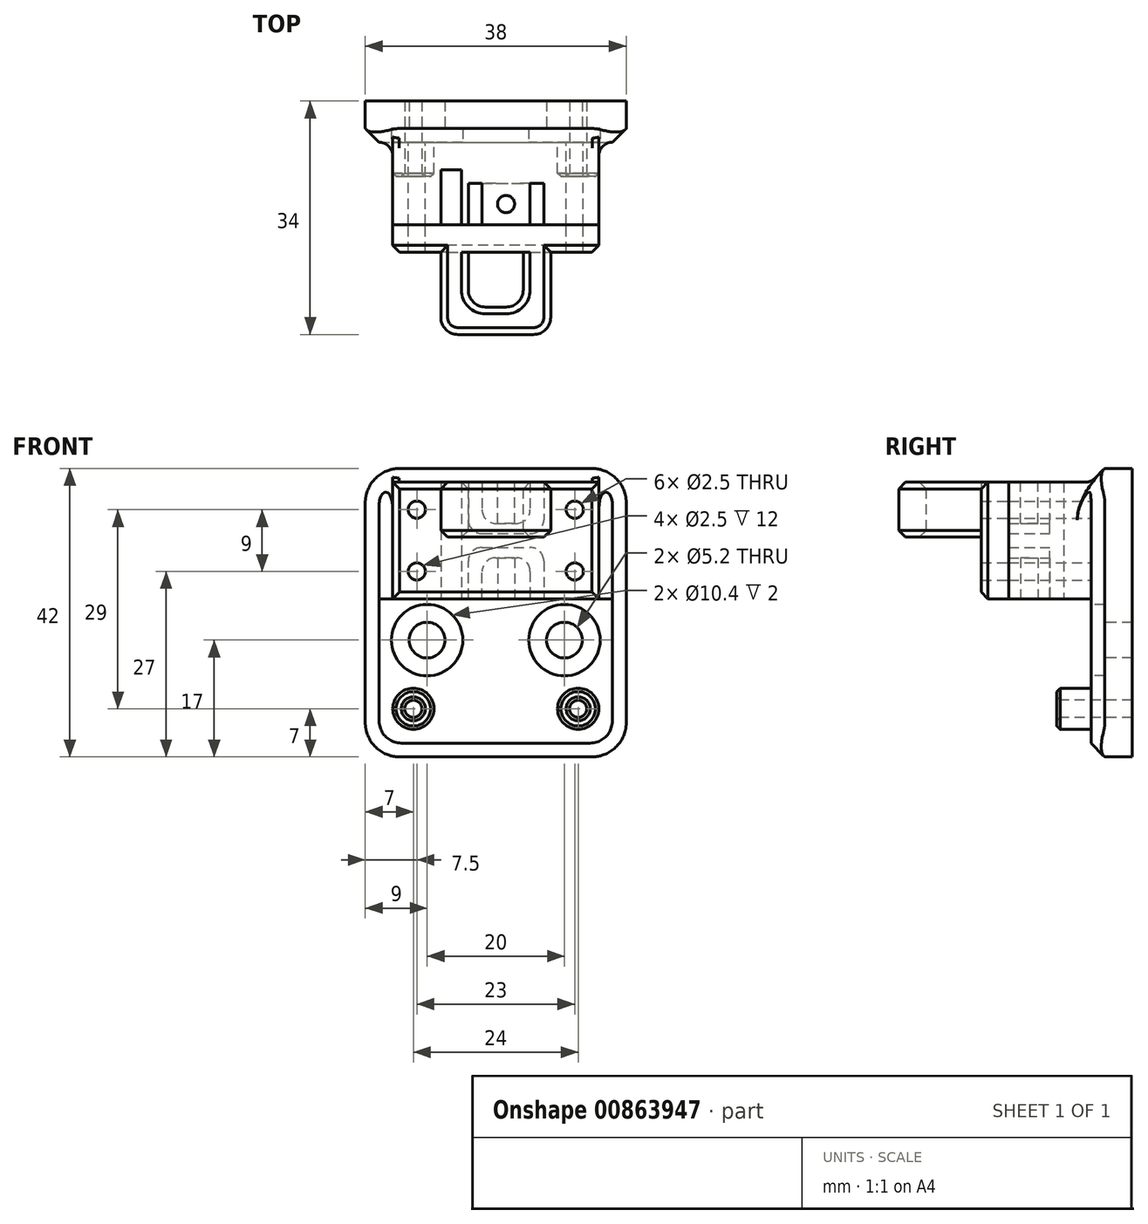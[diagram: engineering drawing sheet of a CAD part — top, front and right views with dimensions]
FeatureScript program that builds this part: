
annotation { "Feature Type Name" : "Feature", "Feature Type Description" : "" }
export const myFeature = defineFeature(function(context is Context, id is Id, definition is map)
    precondition{}
    {
        {
            var Q0;
            Q0=qCreatedBy(makeId("Front.planeOp"),FACE);
            var sketch = newSketch(context, id + "F0", { "sketchPlane" : qUnion([Q0])});
            skLineSegment(sketch, "E0.bottom", {"start": v(-19, 25) * mm, "end": v(19, 25) * mm});
            skLineSegment(sketch, "E0.top", {"start": v(-19, -17) * mm, "end": v(19, -17) * mm});
            skLineSegment(sketch, "E0.left", {"start": v(-19, 25) * mm, "end": v(-19, -17) * mm});
            skLineSegment(sketch, "E0.right", {"start": v(19, 25) * mm, "end": v(19, -17) * mm});
            skCircle(sketch, "E1", {"center": v(-10, 0) * mm, "radius": 2.6 * mm});
            skCircle(sketch, "E2", {"center": v(10, 0) * mm, "radius": 2.6 * mm});
            skCircle(sketch, "E3", {"center": v(-12, -10) * mm, "radius": 3 * mm});
            skCircle(sketch, "E4", {"center": v(-12, -10) * mm, "radius": 1.25 * mm});
            skCircle(sketch, "E5", {"center": v(12, -10) * mm, "radius": 3 * mm});
            skCircle(sketch, "E6", {"center": v(12, -10) * mm, "radius": 1.25 * mm});
            skLineSegment(sketch, "E7", {"start": v(-12, -10) * mm, "end": v(12, -10) * mm, "construction": true});
            skLineSegment(sketch, "E8", {"start": v(-10, 0) * mm, "end": v(10, 0) * mm, "construction": true});
            skLineSegment(sketch, "E9", {"start": v(0, 0) * mm, "end": v(0, -10) * mm, "construction": true});
            skCircle(sketch, "E10", {"center": v(-10, 0) * mm, "radius": 5.2 * mm});
            skCircle(sketch, "E11", {"center": v(10, 0) * mm, "radius": 5.2 * mm});
            skLineSegment(sketch, "E12", {"start": v(0, 25) * mm, "end": v(0, -17) * mm, "construction": true});
            skLineSegment(sketch, "E13.bottom", {"start": v(-15, 23) * mm, "end": v(-8, 23) * mm});
            skLineSegment(sketch, "E13.top", {"start": v(-15, 6) * mm, "end": v(-8, 6) * mm});
            skLineSegment(sketch, "E13.left", {"start": v(-15, 23) * mm, "end": v(-15, 6) * mm});
            skLineSegment(sketch, "E13.right", {"start": v(15, 23) * mm, "end": v(15, 6) * mm});
            skLineSegment(sketch, "E14.bottom", {"start": v(15, 23) * mm, "end": v(7, 23) * mm});
            skLineSegment(sketch, "E14.top", {"start": v(15, 6) * mm, "end": v(7, 6) * mm});
            skLineSegment(sketch, "E14.right", {"start": v(7, 23) * mm, "end": v(7, 6) * mm});
            skLineSegment(sketch, "E15", {"start": v(5, 23) * mm, "end": v(5, 17) * mm});
            skCircle(sketch, "E16", {"center": v(11.5, 19) * mm, "radius": 1.25 * mm});
            skCircle(sketch, "E17", {"center": v(11.5, 10) * mm, "radius": 1.25 * mm});
            skCircle(sketch, "E18", {"center": v(-11.5, 19) * mm, "radius": 1.25 * mm});
            skCircle(sketch, "E19", {"center": v(-11.5, 10) * mm, "radius": 1.25 * mm});
            skLineSegment(sketch, "E20.left", {"start": v(-8, 23) * mm, "end": v(-8, 6) * mm});
            skLineSegment(sketch, "E20.right", {"start": v(-5, 23) * mm, "end": v(-5, 6) * mm});
            skLineSegment(sketch, "E21.bottom", {"start": v(0, 23) * mm, "end": v(-4, 23) * mm});
            skLineSegment(sketch, "E21.right", {"start": v(-4, 23) * mm, "end": v(-4, 15.5) * mm});
            skLineSegment(sketch, "E22.bottom", {"start": v(0, 6) * mm, "end": v(-4, 6) * mm});
            skLineSegment(sketch, "E22.right", {"start": v(-4, 6) * mm, "end": v(-4, 13.5) * mm});
            skLineSegment(sketch, "E23.trimOffspring", {"start": v(5, 12) * mm, "end": v(5, 6) * mm});
            skLineSegment(sketch, "E24.trimOffspring", {"start": v(-5, 23) * mm, "end": v(15, 23) * mm});
            skLineSegment(sketch, "E25.trimOffspring", {"start": v(-4, 15.5) * mm, "end": v(7, 15.5) * mm});
            skLineSegment(sketch, "E26.trimOffspring", {"start": v(-4, 13.5) * mm, "end": v(7, 13.5) * mm});
            skLineSegment(sketch, "E27.trimOffspring", {"start": v(-5, 6) * mm, "end": v(15, 6) * mm});
            skLineSegment(sketch, "E28", {"start": v(-8, 23) * mm, "end": v(-5, 23) * mm});
            skLineSegment(sketch, "E29", {"start": v(-8, 6) * mm, "end": v(-5, 6) * mm});
            skLineSegment(sketch, "E30.trimOffspring", {"start": v(-2, 17) * mm, "end": v(5, 17) * mm});
            skLineSegment(sketch, "E31.trimOffspring", {"start": v(-2, 12) * mm, "end": v(5, 12) * mm});
            skLineSegment(sketch, "E32", {"start": v(-2, 23) * mm, "end": v(-2, 17) * mm});
            skLineSegment(sketch, "E33", {"start": v(5, 23) * mm, "end": v(-2, 23) * mm});
            skLineSegment(sketch, "E34", {"start": v(-2, 6) * mm, "end": v(-2, 12) * mm});
            skSolve(sketch);
        }
        {
            var Q0;
            Q0=makeQuery(id+"F0.imprint","IMPRINT",FACE,{"disambiguationData":[TD([[makeQuery(id+"F0.imprint","IMPRINT",EDGE,{"derivedFrom":sQuery(id+"F0.wireOp",EDGE,"E0.bottom")}),-1.0]])]});
            var Q1;
            Q1=makeQuery(id+"F0.imprint","IMPRINT",FACE,{"disambiguationData":[TD([[makeQuery(id+"F0.imprint","IMPRINT",EDGE,{"derivedFrom":sQuery(id+"F0.wireOp",EDGE,"E3")}),1.0]])]});
            var Q2;
            Q2=makeQuery(id+"F0.imprint","IMPRINT",FACE,{"disambiguationData":[TD([[makeQuery(id+"F0.imprint","IMPRINT",EDGE,{"derivedFrom":sQuery(id+"F0.wireOp",EDGE,"E5")}),1.0]])]});
            var Q3;
            Q3=makeQuery(id+"F0.imprint","IMPRINT",FACE,{"disambiguationData":[TD([[makeQuery(id+"F0.imprint","IMPRINT",EDGE,{"derivedFrom":sQuery(id+"F0.wireOp",EDGE,"E3")}),-1.0]])]});
            var Q4;
            Q4=makeQuery(id+"F0.imprint","IMPRINT",FACE,{"disambiguationData":[TD([[makeQuery(id+"F0.imprint","IMPRINT",EDGE,{"derivedFrom":sQuery(id+"F0.wireOp",EDGE,"E5")}),-1.0]])]});
            var Q5;
            {var subQ1=sQuery(id+"F0.wireOp",EDGE,"KE5ROvnR-nKlG-dR7P-LUSN-xowkLqCSfsb7.bottom");Q5=makeQuery(id+"F0.imprint","IMPRINT",FACE,{"disambiguationData":[TD([[makeQuery(id+"F0.imprint","IMPRINT",EDGE,{"derivedFrom":subQ1}),-1.0]])]});}
            var Q6;
            Q6=makeQuery(id+"F0.imprint","IMPRINT",FACE,{"disambiguationData":[TD([[makeQuery(id+"F0.imprint","IMPRINT",EDGE,{"derivedFrom":sQuery(id+"F0.wireOp",EDGE,"E1")}),-1.0]])]});
            var Q7;
            Q7=makeQuery(id+"F0.imprint","IMPRINT",FACE,{"disambiguationData":[TD([[makeQuery(id+"F0.imprint","IMPRINT",EDGE,{"derivedFrom":sQuery(id+"F0.wireOp",EDGE,"E2")}),-1.0]])]});
            var Q8;
            Q8=makeQuery(id+"F0.imprint","IMPRINT",FACE,{"disambiguationData":[TD([[makeQuery(id+"F0.imprint","IMPRINT",EDGE,{"derivedFrom":sQuery(id+"F0.wireOp",EDGE,"7S5Ky6bi-a4UI-zwk8-JNnX-DnWfXbXULz1x.bottom")}),-1.0]])]});
            var Q9;
            {var subQ4=sQuery(id+"F0.wireOp",EDGE,"0DTDjkwD-hyOw-EM9f-qp8T-9hL6FurCrIPk.top");Q9=makeQuery(id+"F0.imprint","IMPRINT",FACE,{"disambiguationData":[TD([[makeQuery(id+"F0.imprint","IMPRINT",EDGE,{"derivedFrom":subQ4}),1.0]])]});}
            var Q10;
            {var subQ0=sQuery(id+"F0.wireOp",EDGE,"0DTDjkwD-hyOw-EM9f-qp8T-9hL6FurCrIPk.bottom");Q10=makeQuery(id+"F0.imprint","IMPRINT",FACE,{"disambiguationData":[TD([[makeQuery(id+"F0.imprint","IMPRINT",EDGE,{"derivedFrom":subQ0}),1.0]])]});}
            var Q11;
            {var subQ0=sQuery(id+"F0.wireOp",EDGE,"0K5foB9j-LH2L-z9Mt-iZWl-Or50KG6ktl6Q.bottom");Q11=makeQuery(id+"F0.imprint","IMPRINT",FACE,{"disambiguationData":[TD([[makeQuery(id+"F0.imprint","IMPRINT",EDGE,{"derivedFrom":subQ0}),1.0]])]});}
            var Q12;
            {var subQ4=sQuery(id+"F0.wireOp",EDGE,"0K5foB9j-LH2L-z9Mt-iZWl-Or50KG6ktl6Q.top");Q12=makeQuery(id+"F0.imprint","IMPRINT",FACE,{"disambiguationData":[TD([[makeQuery(id+"F0.imprint","IMPRINT",EDGE,{"derivedFrom":subQ4}),1.0]])]});}
            var Q13;
            {var subQ0=sQuery(id+"F0.wireOp",EDGE,"0DTDjkwD-hyOw-EM9f-qp8T-9hL6FurCrIPk.bottom");Q13=makeQuery(id+"F0.imprint","IMPRINT",FACE,{"disambiguationData":[TD([[makeQuery(id+"F0.imprint","IMPRINT",EDGE,{"derivedFrom":subQ0}),-1.0]])]});}
            var Q14;
            {var subQ0=sQuery(id+"F0.wireOp",EDGE,"0K5foB9j-LH2L-z9Mt-iZWl-Or50KG6ktl6Q.bottom");Q14=makeQuery(id+"F0.imprint","IMPRINT",FACE,{"disambiguationData":[TD([[makeQuery(id+"F0.imprint","IMPRINT",EDGE,{"derivedFrom":subQ0}),-1.0]])]});}
            var Q15;
            {var subQ0=sQuery(id+"F0.wireOp",EDGE,"8f55sNTK-9v3j-GzLA-QblO-wIgXxyOoYHQr.bottom");Q15=makeQuery(id+"F0.imprint","IMPRINT",FACE,{"disambiguationData":[TD([[makeQuery(id+"F0.imprint","IMPRINT",EDGE,{"derivedFrom":subQ0}),-1.0]])]});}
            var Q16;
            {var subQ0=sQuery(id+"F0.wireOp",EDGE,"4fc9d737-95ee-41e9-862a-7390b013f1c5");var subQ1=sQuery(id+"F0.wireOp",EDGE,"8f55sNTK-9v3j-GzLA-QblO-wIgXxyOoYHQr.left");var subQ2=makeQuery(id+"F0.imprint","INTERSECT",VERTEX,{"disambiguationData":[OD(0.0)],"derivedFrom":[subQ1,subQ0]});Q16=makeQuery(id+"F0.imprint","IMPRINT",FACE,{"disambiguationData":[TD([[makeQuery(id+"F0.imprint","IMPRINT",EDGE,{"disambiguationData":[TD([[subQ2,-1.0]])],"derivedFrom":subQ1}),-1.0]])]});}
            var Q17;
            {var subQ0=sQuery(id+"F0.wireOp",EDGE,"4fc9d737-95ee-41e9-862a-7390b013f1c5");var subQ1=sQuery(id+"F0.wireOp",EDGE,"8f55sNTK-9v3j-GzLA-QblO-wIgXxyOoYHQr.left");var subQ2=makeQuery(id+"F0.imprint","INTERSECT",VERTEX,{"disambiguationData":[OD(0.0)],"derivedFrom":[subQ1,subQ0]});Q17=makeQuery(id+"F0.imprint","IMPRINT",FACE,{"disambiguationData":[TD([[makeQuery(id+"F0.imprint","IMPRINT",EDGE,{"disambiguationData":[TD([[subQ2,-1.0]])],"derivedFrom":subQ1}),1.0]])]});}
            var Q18;
            {var subQ0=sQuery(id+"F0.wireOp",EDGE,"4fc9d737-95ee-41e9-862a-7390b013f1c5");var subQ1=sQuery(id+"F0.wireOp",EDGE,"8f55sNTK-9v3j-GzLA-QblO-wIgXxyOoYHQr.left");var subQ2=makeQuery(id+"F0.imprint","INTERSECT",VERTEX,{"disambiguationData":[OD(1.0)],"derivedFrom":[subQ1,subQ0]});Q18=makeQuery(id+"F0.imprint","IMPRINT",FACE,{"disambiguationData":[TD([[makeQuery(id+"F0.imprint","IMPRINT",EDGE,{"disambiguationData":[TD([[subQ2,-1.0]])],"derivedFrom":subQ1}),1.0]])]});}
            var Q19;
            {var subQ0=sQuery(id+"F0.wireOp",EDGE,"InRWTkDz-I3E0-UDBL-FPYz-RPvXa85QaQg0");var subQ1=sQuery(id+"F0.wireOp",EDGE,"8f55sNTK-9v3j-GzLA-QblO-wIgXxyOoYHQr.right");var subQ2=makeQuery(id+"F0.imprint","INTERSECT",VERTEX,{"disambiguationData":[OD(0.0)],"derivedFrom":[subQ1,subQ0]});Q19=makeQuery(id+"F0.imprint","IMPRINT",FACE,{"disambiguationData":[TD([[makeQuery(id+"F0.imprint","IMPRINT",EDGE,{"disambiguationData":[TD([[subQ2,-1.0]])],"derivedFrom":subQ1}),-1.0]])]});}
            var Q20;
            {var subQ0=sQuery(id+"F0.wireOp",EDGE,"InRWTkDz-I3E0-UDBL-FPYz-RPvXa85QaQg0");var subQ1=sQuery(id+"F0.wireOp",EDGE,"8f55sNTK-9v3j-GzLA-QblO-wIgXxyOoYHQr.right");var subQ2=makeQuery(id+"F0.imprint","INTERSECT",VERTEX,{"disambiguationData":[OD(0.0)],"derivedFrom":[subQ1,subQ0]});Q20=makeQuery(id+"F0.imprint","IMPRINT",FACE,{"disambiguationData":[TD([[makeQuery(id+"F0.imprint","IMPRINT",EDGE,{"disambiguationData":[TD([[subQ2,-1.0]])],"derivedFrom":subQ1}),1.0]])]});}
            var Q21;
            {var subQ0=sQuery(id+"F0.wireOp",EDGE,"8f55sNTK-9v3j-GzLA-QblO-wIgXxyOoYHQr.top");Q21=makeQuery(id+"F0.imprint","IMPRINT",FACE,{"disambiguationData":[TD([[makeQuery(id+"F0.imprint","IMPRINT",EDGE,{"derivedFrom":subQ0}),1.0]])]});}
            var Q22;
            {var subQ0=sQuery(id+"F0.wireOp",EDGE,"E13.bottom");Q22=makeQuery(id+"F0.imprint","IMPRINT",FACE,{"disambiguationData":[TD([[makeQuery(id+"F0.imprint","IMPRINT",EDGE,{"derivedFrom":subQ0}),-1.0]])]});}
            var Q23;
            Q23=makeQuery(id+"F0.imprint","IMPRINT",FACE,{"disambiguationData":[TD([[makeQuery(id+"F0.imprint","IMPRINT",EDGE,{"derivedFrom":sQuery(id+"F0.wireOp",EDGE,"JneHIZzw-hAGB-WEz8-UXSy-7EQ4Qx5uxvCV.bottom")}),-1.0]])]});
            var Q24;
            {var subQ0=sQuery(id+"F0.wireOp",EDGE,"JneHIZzw-hAGB-WEz8-UXSy-7EQ4Qx5uxvCV.top");Q24=makeQuery(id+"F0.imprint","IMPRINT",FACE,{"disambiguationData":[TD([[makeQuery(id+"F0.imprint","IMPRINT",EDGE,{"derivedFrom":subQ0}),-1.0]])]});}
            var Q25;
            Q25=makeQuery(id+"F0.imprint","IMPRINT",FACE,{"disambiguationData":[TD([[makeQuery(id+"F0.imprint","IMPRINT",EDGE,{"derivedFrom":sQuery(id+"F0.wireOp",EDGE,"op12IUDS-wtd1-xCTw-FGPv-pRemV9Gbpv2m.bottom")}),-1.0]])]});
            var Q26;
            {var subQ0=sQuery(id+"F0.wireOp",EDGE,"E13.top");Q26=makeQuery(id+"F0.imprint","IMPRINT",FACE,{"disambiguationData":[TD([[makeQuery(id+"F0.imprint","IMPRINT",EDGE,{"derivedFrom":subQ0}),1.0]])]});}
            var Q27;
            Q27=makeQuery(id+"F0.imprint","IMPRINT",FACE,{"disambiguationData":[TD([[makeQuery(id+"F0.imprint","IMPRINT",EDGE,{"derivedFrom":sQuery(id+"F0.wireOp",EDGE,"E14.bottom")}),1.0]])]});
            var Q28;
            {var subQ0=sQuery(id+"F0.wireOp",EDGE,"WXd5efYa-JbfL-IF1L-SslL-BDGKgb6K0dqY");Q28=makeQuery(id+"F0.imprint","IMPRINT",FACE,{"disambiguationData":[TD([[makeQuery(id+"F0.imprint","IMPRINT",EDGE,{"derivedFrom":subQ0}),-1.0]])]});}
            var Q29;
            {var subQ0=sQuery(id+"F0.wireOp",EDGE,"o5i0NS2g-xdNk-XHE3-dkdj-B6CzDAg9Y3Px");Q29=makeQuery(id+"F0.imprint","IMPRINT",FACE,{"disambiguationData":[TD([[makeQuery(id+"F0.imprint","IMPRINT",EDGE,{"derivedFrom":subQ0}),-1.0]])]});}
            var Q30;
            {var subQ0=sQuery(id+"F0.wireOp",EDGE,"a3aYjSOv-KGgK-Pzp2-STLL-ZoR566E2SG2L");Q30=makeQuery(id+"F0.imprint","IMPRINT",FACE,{"disambiguationData":[TD([[makeQuery(id+"F0.imprint","IMPRINT",EDGE,{"derivedFrom":subQ0}),-1.0]])]});}
            var Q31;
            {var subQ0=sQuery(id+"F0.wireOp",EDGE,"E14.right");Q31=makeQuery(id+"F0.imprint","IMPRINT",FACE,{"disambiguationData":[TD([[makeQuery(id+"F0.imprint","IMPRINT",EDGE,{"derivedFrom":subQ0}),-1.0]])]});}
            var Q32;
            Q32=makeQuery(id+"F0.imprint","IMPRINT",FACE,{"disambiguationData":[TD([[makeQuery(id+"F0.imprint","IMPRINT",EDGE,{"derivedFrom":sQuery(id+"F0.wireOp",EDGE,"E18")}),1.0]])]});
            var Q33;
            Q33=makeQuery(id+"F0.imprint","IMPRINT",FACE,{"disambiguationData":[TD([[makeQuery(id+"F0.imprint","IMPRINT",EDGE,{"derivedFrom":sQuery(id+"F0.wireOp",EDGE,"E16")}),1.0]])]});
            var Q34;
            Q34=makeQuery(id+"F0.imprint","IMPRINT",FACE,{"disambiguationData":[TD([[makeQuery(id+"F0.imprint","IMPRINT",EDGE,{"derivedFrom":sQuery(id+"F0.wireOp",EDGE,"E17")}),1.0]])]});
            var Q35;
            Q35=makeQuery(id+"F0.imprint","IMPRINT",FACE,{"disambiguationData":[TD([[makeQuery(id+"F0.imprint","IMPRINT",EDGE,{"derivedFrom":sQuery(id+"F0.wireOp",EDGE,"E19")}),1.0]])]});
            var Q36;
            Q36=makeQuery(id+"F0.imprint","IMPRINT",FACE,{"disambiguationData":[TD([[makeQuery(id+"F0.imprint","IMPRINT",EDGE,{"derivedFrom":sQuery(id+"F0.wireOp",EDGE,"E18")}),-1.0]])]});
            var Q37;
            {var subQ5=sQuery(id+"F0.wireOp",EDGE,"E20.bottom");Q37=makeQuery(id+"F0.imprint","IMPRINT",FACE,{"disambiguationData":[TD([[makeQuery(id+"F0.imprint","IMPRINT",EDGE,{"derivedFrom":subQ5}),-1.0]])]});}
            var Q38;
            {var subQ5=sQuery(id+"F0.wireOp",EDGE,"E20.top");Q38=makeQuery(id+"F0.imprint","IMPRINT",FACE,{"disambiguationData":[TD([[makeQuery(id+"F0.imprint","IMPRINT",EDGE,{"derivedFrom":subQ5}),1.0]])]});}
            var Q39;
            Q39=makeQuery(id+"F0.imprint","IMPRINT",FACE,{"disambiguationData":[TD([[makeQuery(id+"F0.imprint","IMPRINT",EDGE,{"derivedFrom":sQuery(id+"F0.wireOp",EDGE,"E19")}),-1.0]])]});
            var Q40;
            {var subQ0=sQuery(id+"F0.wireOp",EDGE,"o5i0NS2g-xdNk-XHE3-dkdj-B6CzDAg9Y3Px");var subQ1=sQuery(id+"F0.wireOp",EDGE,"E13.left");var subQ2=makeQuery(id+"F0.imprint","INTERSECT",VERTEX,{"derivedFrom":[subQ1,subQ0]});Q40=makeQuery(id+"F0.imprint","IMPRINT",FACE,{"disambiguationData":[TD([[makeQuery(id+"F0.imprint","IMPRINT",EDGE,{"disambiguationData":[TD([[subQ2,-1.0]])],"derivedFrom":subQ1}),1.0]])]});}
            var Q41;
            {var subQ0=sQuery(id+"F0.wireOp",EDGE,"E20.left");var subQ1=sQuery(id+"F0.wireOp",EDGE,"o5i0NS2g-xdNk-XHE3-dkdj-B6CzDAg9Y3Px");var subQ2=makeQuery(id+"F0.imprint","INTERSECT",VERTEX,{"derivedFrom":[subQ1,subQ0]});Q41=makeQuery(id+"F0.imprint","IMPRINT",FACE,{"disambiguationData":[TD([[makeQuery(id+"F0.imprint","IMPRINT",EDGE,{"disambiguationData":[TD([[subQ2,-1.0]])],"derivedFrom":subQ1}),-1.0]])]});}
            var Q42;
            Q42=makeQuery(id+"F0.imprint","IMPRINT",FACE,{"disambiguationData":[TD([[makeQuery(id+"F0.imprint","IMPRINT",EDGE,{"derivedFrom":sQuery(id+"F0.wireOp",EDGE,"E21.bottom")}),1.0]])]});
            var Q43;
            Q43=makeQuery(id+"F0.imprint","IMPRINT",FACE,{"disambiguationData":[TD([[makeQuery(id+"F0.imprint","IMPRINT",EDGE,{"derivedFrom":sQuery(id+"F0.wireOp",EDGE,"E22.bottom")}),-1.0]])]});
            var Q44;
            {var subQ0=sQuery(id+"F0.wireOp",EDGE,"E22.top");Q44=makeQuery(id+"F0.imprint","IMPRINT",FACE,{"disambiguationData":[TD([[makeQuery(id+"F0.imprint","IMPRINT",EDGE,{"derivedFrom":subQ0}),-1.0]])]});}
            var Q45;
            {var subQ7=sQuery(id+"F0.wireOp",EDGE,"E21.top");Q45=makeQuery(id+"F0.imprint","IMPRINT",FACE,{"disambiguationData":[TD([[makeQuery(id+"F0.imprint","IMPRINT",EDGE,{"derivedFrom":subQ7}),1.0]])]});}
            var Q46;
            {var subQ0=sQuery(id+"F0.wireOp",EDGE,"E15");Q46=makeQuery(id+"F0.imprint","IMPRINT",FACE,{"disambiguationData":[TD([[makeQuery(id+"F0.imprint","IMPRINT",EDGE,{"derivedFrom":subQ0}),-1.0]])]});}
            var Q47;
            {var subQ5=sQuery(id+"F0.wireOp",EDGE,"E21.right");Q47=makeQuery(id+"F0.imprint","IMPRINT",FACE,{"disambiguationData":[TD([[makeQuery(id+"F0.imprint","IMPRINT",EDGE,{"derivedFrom":subQ5}),-1.0]])]});}
            var Q48;
            {var subQ0=sQuery(id+"F0.wireOp",EDGE,"afa951f2-33ce-410b-8e7f-cae244085d47.trimOffspring");var subQ1=sQuery(id+"F0.wireOp",EDGE,"E20.right");var subQ2=makeQuery(id+"F0.imprint","INTERSECT",VERTEX,{"derivedFrom":[subQ1,subQ0]});Q48=makeQuery(id+"F0.imprint","IMPRINT",FACE,{"disambiguationData":[TD([[makeQuery(id+"F0.imprint","IMPRINT",EDGE,{"disambiguationData":[TD([[subQ2,-1.0]])],"derivedFrom":subQ1}),1.0]])]});}
            var Q49;
            {var subQ0=sQuery(id+"F0.wireOp",EDGE,"E25.trimOffspring");var subQ1=sQuery(id+"F0.wireOp",EDGE,"E20.right");var subQ2=makeQuery(id+"F0.imprint","INTERSECT",VERTEX,{"derivedFrom":[subQ1,subQ0]});Q49=makeQuery(id+"F0.imprint","IMPRINT",FACE,{"disambiguationData":[TD([[makeQuery(id+"F0.imprint","IMPRINT",EDGE,{"disambiguationData":[TD([[subQ2,-1.0]])],"derivedFrom":subQ1}),1.0]])]});}
            var Q50;
            {var subQ0=sQuery(id+"F0.wireOp",EDGE,"E26.trimOffspring");var subQ1=sQuery(id+"F0.wireOp",EDGE,"E20.right");var subQ2=makeQuery(id+"F0.imprint","INTERSECT",VERTEX,{"derivedFrom":[subQ1,subQ0]});Q50=makeQuery(id+"F0.imprint","IMPRINT",FACE,{"disambiguationData":[TD([[makeQuery(id+"F0.imprint","IMPRINT",EDGE,{"disambiguationData":[TD([[subQ2,-1.0]])],"derivedFrom":subQ1}),1.0]])]});}
            var Q51;
            {var subQ5=sQuery(id+"F0.wireOp",EDGE,"E22.right");Q51=makeQuery(id+"F0.imprint","IMPRINT",FACE,{"disambiguationData":[TD([[makeQuery(id+"F0.imprint","IMPRINT",EDGE,{"derivedFrom":subQ5}),1.0]])]});}
            var Q52;
            {var subQ0=sQuery(id+"F0.wireOp",EDGE,"E22.left");Q52=makeQuery(id+"F0.imprint","IMPRINT",FACE,{"disambiguationData":[TD([[makeQuery(id+"F0.imprint","IMPRINT",EDGE,{"derivedFrom":subQ0}),1.0]])]});}
            var Q53;
            {var subQ0=sQuery(id+"F0.wireOp",EDGE,"E22.left");Q53=makeQuery(id+"F0.imprint","IMPRINT",FACE,{"disambiguationData":[TD([[makeQuery(id+"F0.imprint","IMPRINT",EDGE,{"derivedFrom":subQ0}),-1.0]])]});}
            var Q54;
            {var subQ5=sQuery(id+"F0.wireOp",EDGE,"451da361-41a1-4976-9240-72445684a393.trimOffspring");Q54=makeQuery(id+"F0.imprint","IMPRINT",FACE,{"disambiguationData":[TD([[makeQuery(id+"F0.imprint","IMPRINT",EDGE,{"derivedFrom":subQ5}),-1.0]])]});}
            var Q55;
            {var subQ2=sQuery(id+"F0.wireOp",EDGE,"E13.right");Q55=makeQuery(id+"F0.imprint","IMPRINT",FACE,{"disambiguationData":[TD([[makeQuery(id+"F0.imprint","IMPRINT",EDGE,{"derivedFrom":subQ2}),-1.0]])]});}
            var Q56;
            {var subQ0=sQuery(id+"F0.wireOp",EDGE,"E21.left");Q56=makeQuery(id+"F0.imprint","IMPRINT",FACE,{"disambiguationData":[TD([[makeQuery(id+"F0.imprint","IMPRINT",EDGE,{"derivedFrom":subQ0}),-1.0]])]});}
            var Q57;
            {var subQ6=sQuery(id+"F0.wireOp",EDGE,"E28");Q57=makeQuery(id+"F0.imprint","IMPRINT",FACE,{"disambiguationData":[TD([[makeQuery(id+"F0.imprint","IMPRINT",EDGE,{"derivedFrom":subQ6}),-1.0]])]});}
            var Q58;
            {var subQ3=sQuery(id+"F0.wireOp",EDGE,"E23.trimOffspring");Q58=makeQuery(id+"F0.imprint","IMPRINT",FACE,{"disambiguationData":[TD([[makeQuery(id+"F0.imprint","IMPRINT",EDGE,{"derivedFrom":subQ3}),-1.0]])]});}
            extrude(context, id + "F1", {"entities" : qUnion([Q0, Q1, Q2, Q3, Q4, Q5, Q6, Q7, Q8, Q9, Q10, Q11, Q12, Q13, Q14, Q15, Q16, Q17, Q18, Q19, Q20, Q21, Q22, Q23, Q24, Q25, Q26, Q27, Q28, Q29, Q30, Q31, Q32, Q33, Q34, Q35, Q36, Q37, Q38, Q39, Q40, Q41, Q42, Q43, Q44, Q45, Q46, Q47, Q48, Q49, Q50, Q51, Q52, Q53, Q54, Q55, Q56, Q57, Q58]), "oppositeDirection" : true, "depth" : 6 * mm, "offsetDistance" : 25 * mm});
        }
        {
            var Q0;
            Q0=makeQuery(id+"F0.imprint","IMPRINT",FACE,{"disambiguationData":[TD([[makeQuery(id+"F0.imprint","IMPRINT",EDGE,{"derivedFrom":sQuery(id+"F0.wireOp",EDGE,"E1")}),-1.0]])]});
            var Q1;
            Q1=makeQuery(id+"F0.imprint","IMPRINT",FACE,{"disambiguationData":[TD([[makeQuery(id+"F0.imprint","IMPRINT",EDGE,{"derivedFrom":sQuery(id+"F0.wireOp",EDGE,"E2")}),-1.0]])]});
            extrude(context, id + "F2", {"entities" : qUnion([Q0, Q1]), "operationType" : NewBodyOperationType.REMOVE, "oppositeDirection" : true, "depth" : 2 * mm, "offsetDistance" : 25 * mm});
        }
        {
            var Q0;
            Q0=makeQuery(id+"F0.imprint","IMPRINT",FACE,{"disambiguationData":[TD([[makeQuery(id+"F0.imprint","IMPRINT",EDGE,{"derivedFrom":sQuery(id+"F0.wireOp",EDGE,"E3")}),1.0]])]});
            var Q1;
            Q1=makeQuery(id+"F0.imprint","IMPRINT",FACE,{"disambiguationData":[TD([[makeQuery(id+"F0.imprint","IMPRINT",EDGE,{"derivedFrom":sQuery(id+"F0.wireOp",EDGE,"E5")}),1.0]])]});
            extrude(context, id + "F3", {"entities" : qUnion([Q0, Q1]), "operationType" : NewBodyOperationType.ADD, "depth" : 5 * mm, "offsetDistance" : 25 * mm});
        }
        {
            var Q0;
            {var subQ0=sQuery(id+"F0.wireOp",EDGE,"WXd5efYa-JbfL-IF1L-SslL-BDGKgb6K0dqY");var subQ1=sQuery(id+"F0.wireOp",EDGE,"E13.left");var subQ2=makeQuery(id+"F0.imprint","INTERSECT",VERTEX,{"derivedFrom":[subQ1,subQ0]});Q0=makeQuery(id+"F0.imprint","IMPRINT",FACE,{"disambiguationData":[TD([[makeQuery(id+"F0.imprint","IMPRINT",EDGE,{"disambiguationData":[TD([[subQ2,-1.0]])],"derivedFrom":subQ1}),1.0]])]});}
            var Q1;
            {var subQ0=sQuery(id+"F0.wireOp",EDGE,"WXd5efYa-JbfL-IF1L-SslL-BDGKgb6K0dqY");var subQ1=sQuery(id+"F0.wireOp",EDGE,"E15");var subQ2=makeQuery(id+"F0.imprint","INTERSECT",VERTEX,{"derivedFrom":[subQ1,subQ0]});Q1=makeQuery(id+"F0.imprint","IMPRINT",FACE,{"disambiguationData":[TD([[makeQuery(id+"F0.imprint","IMPRINT",EDGE,{"disambiguationData":[TD([[subQ2,-1.0]])],"derivedFrom":subQ1}),-1.0]])]});}
            var Q2;
            {var subQ3=sQuery(id+"F0.wireOp",EDGE,"E21.right");Q2=makeQuery(id+"F0.imprint","IMPRINT",FACE,{"disambiguationData":[TD([[makeQuery(id+"F0.imprint","IMPRINT",EDGE,{"derivedFrom":subQ3}),-1.0]])]});}
            var Q3;
            {var subQ3=sQuery(id+"F0.wireOp",EDGE,"E21.left");Q3=makeQuery(id+"F0.imprint","IMPRINT",FACE,{"disambiguationData":[TD([[makeQuery(id+"F0.imprint","IMPRINT",EDGE,{"derivedFrom":subQ3}),1.0]])]});}
            var Q4;
            {var subQ3=sQuery(id+"F0.wireOp",EDGE,"E22.right");Q4=makeQuery(id+"F0.imprint","IMPRINT",FACE,{"disambiguationData":[TD([[makeQuery(id+"F0.imprint","IMPRINT",EDGE,{"derivedFrom":subQ3}),1.0]])]});}
            var Q5;
            {var subQ3=sQuery(id+"F0.wireOp",EDGE,"E22.left");Q5=makeQuery(id+"F0.imprint","IMPRINT",FACE,{"disambiguationData":[TD([[makeQuery(id+"F0.imprint","IMPRINT",EDGE,{"derivedFrom":subQ3}),-1.0]])]});}
            var Q6;
            Q6=makeQuery(id+"F0.imprint","IMPRINT",FACE,{"disambiguationData":[TD([[makeQuery(id+"F0.imprint","IMPRINT",EDGE,{"derivedFrom":sQuery(id+"F0.wireOp",EDGE,"E14.bottom")}),1.0]])]});
            var Q7;
            Q7=makeQuery(id+"F0.imprint","IMPRINT",FACE,{"disambiguationData":[TD([[makeQuery(id+"F0.imprint","IMPRINT",EDGE,{"derivedFrom":sQuery(id+"F0.wireOp",EDGE,"E18")}),-1.0]])]});
            var Q8;
            Q8=makeQuery(id+"F0.imprint","IMPRINT",FACE,{"disambiguationData":[TD([[makeQuery(id+"F0.imprint","IMPRINT",EDGE,{"derivedFrom":sQuery(id+"F0.wireOp",EDGE,"E19")}),-1.0]])]});
            var Q9;
            {var subQ0=sQuery(id+"F0.wireOp",EDGE,"o5i0NS2g-xdNk-XHE3-dkdj-B6CzDAg9Y3Px");var subQ1=sQuery(id+"F0.wireOp",EDGE,"E13.left");var subQ2=makeQuery(id+"F0.imprint","INTERSECT",VERTEX,{"derivedFrom":[subQ1,subQ0]});Q9=makeQuery(id+"F0.imprint","IMPRINT",FACE,{"disambiguationData":[TD([[makeQuery(id+"F0.imprint","IMPRINT",EDGE,{"disambiguationData":[TD([[subQ2,-1.0]])],"derivedFrom":subQ1}),1.0]])]});}
            var Q10;
            {var subQ0=sQuery(id+"F0.wireOp",EDGE,"a3aYjSOv-KGgK-Pzp2-STLL-ZoR566E2SG2L");var subQ1=sQuery(id+"F0.wireOp",EDGE,"E13.left");var subQ2=makeQuery(id+"F0.imprint","INTERSECT",VERTEX,{"derivedFrom":[subQ1,subQ0]});Q10=makeQuery(id+"F0.imprint","IMPRINT",FACE,{"disambiguationData":[TD([[makeQuery(id+"F0.imprint","IMPRINT",EDGE,{"disambiguationData":[TD([[subQ2,-1.0]])],"derivedFrom":subQ1}),1.0]])]});}
            var Q11;
            {var subQ3=sQuery(id+"F0.wireOp",EDGE,"E20.right");var subQ5=sQuery(id+"F0.wireOp",EDGE,"WXd5efYa-JbfL-IF1L-SslL-BDGKgb6K0dqY");var subQ6=makeQuery(id+"F0.imprint","INTERSECT",VERTEX,{"derivedFrom":[subQ5,subQ3]});Q11=makeQuery(id+"F0.imprint","IMPRINT",FACE,{"disambiguationData":[TD([[makeQuery(id+"F0.imprint","IMPRINT",EDGE,{"disambiguationData":[TD([[subQ6,-1.0]])],"derivedFrom":subQ5}),1.0]])]});}
            var Q12;
            {var subQ0=sQuery(id+"F0.wireOp",EDGE,"E20.right");var subQ1=sQuery(id+"F0.wireOp",EDGE,"WXd5efYa-JbfL-IF1L-SslL-BDGKgb6K0dqY");var subQ2=makeQuery(id+"F0.imprint","INTERSECT",VERTEX,{"derivedFrom":[subQ1,subQ0]});Q12=makeQuery(id+"F0.imprint","IMPRINT",FACE,{"disambiguationData":[TD([[makeQuery(id+"F0.imprint","IMPRINT",EDGE,{"disambiguationData":[TD([[subQ2,-1.0]])],"derivedFrom":subQ1}),-1.0]])]});}
            var Q13;
            {var subQ0=sQuery(id+"F0.wireOp",EDGE,"E20.right");var subQ1=sQuery(id+"F0.wireOp",EDGE,"a3aYjSOv-KGgK-Pzp2-STLL-ZoR566E2SG2L");var subQ2=makeQuery(id+"F0.imprint","INTERSECT",VERTEX,{"derivedFrom":[subQ1,subQ0]});Q13=makeQuery(id+"F0.imprint","IMPRINT",FACE,{"disambiguationData":[TD([[makeQuery(id+"F0.imprint","IMPRINT",EDGE,{"disambiguationData":[TD([[subQ2,-1.0]])],"derivedFrom":subQ1}),-1.0]])]});}
            var Q14;
            {var subQ0=sQuery(id+"F0.wireOp",EDGE,"451da361-41a1-4976-9240-72445684a393.trimOffspring");Q14=makeQuery(id+"F0.imprint","IMPRINT",FACE,{"disambiguationData":[TD([[makeQuery(id+"F0.imprint","IMPRINT",EDGE,{"derivedFrom":subQ0}),-1.0]])]});}
            var Q15;
            {var subQ2=sQuery(id+"F0.wireOp",EDGE,"E13.right");Q15=makeQuery(id+"F0.imprint","IMPRINT",FACE,{"disambiguationData":[TD([[makeQuery(id+"F0.imprint","IMPRINT",EDGE,{"derivedFrom":subQ2}),-1.0]])]});}
            var Q16;
            {var subQ0=sQuery(id+"F0.wireOp",EDGE,"afa951f2-33ce-410b-8e7f-cae244085d47.trimOffspring");var subQ1=sQuery(id+"F0.wireOp",EDGE,"E20.right");var subQ2=makeQuery(id+"F0.imprint","INTERSECT",VERTEX,{"derivedFrom":[subQ1,subQ0]});Q16=makeQuery(id+"F0.imprint","IMPRINT",FACE,{"disambiguationData":[TD([[makeQuery(id+"F0.imprint","IMPRINT",EDGE,{"disambiguationData":[TD([[subQ2,-1.0]])],"derivedFrom":subQ1}),1.0]])]});}
            var Q17;
            {var subQ0=sQuery(id+"F0.wireOp",EDGE,"E25.trimOffspring");var subQ1=sQuery(id+"F0.wireOp",EDGE,"E20.right");var subQ2=makeQuery(id+"F0.imprint","INTERSECT",VERTEX,{"derivedFrom":[subQ1,subQ0]});Q17=makeQuery(id+"F0.imprint","IMPRINT",FACE,{"disambiguationData":[TD([[makeQuery(id+"F0.imprint","IMPRINT",EDGE,{"disambiguationData":[TD([[subQ2,-1.0]])],"derivedFrom":subQ1}),1.0]])]});}
            var Q18;
            {var subQ0=sQuery(id+"F0.wireOp",EDGE,"E26.trimOffspring");var subQ1=sQuery(id+"F0.wireOp",EDGE,"E20.right");var subQ2=makeQuery(id+"F0.imprint","INTERSECT",VERTEX,{"derivedFrom":[subQ1,subQ0]});Q18=makeQuery(id+"F0.imprint","IMPRINT",FACE,{"disambiguationData":[TD([[makeQuery(id+"F0.imprint","IMPRINT",EDGE,{"disambiguationData":[TD([[subQ2,-1.0]])],"derivedFrom":subQ1}),1.0]])]});}
            var Q19;
            {var subQ3=sQuery(id+"F0.wireOp",EDGE,"E23.trimOffspring");Q19=makeQuery(id+"F0.imprint","IMPRINT",FACE,{"disambiguationData":[TD([[makeQuery(id+"F0.imprint","IMPRINT",EDGE,{"derivedFrom":subQ3}),-1.0]])]});}
            extrude(context, id + "F4", {"entities" : qUnion([Q0, Q1, Q2, Q3, Q4, Q5, Q6, Q7, Q8, Q9, Q10, Q11, Q12, Q13, Q14, Q15, Q16, Q17, Q18, Q19]), "operationType" : NewBodyOperationType.ADD, "depth" : 12 * mm, "offsetDistance" : 25 * mm});
        }
        {
            var Q0;
            {var subQ0=sQuery(id+"F0.wireOp",EDGE,"E14.right");Q0=makeQuery(id+"F0.imprint","IMPRINT",FACE,{"disambiguationData":[TD([[makeQuery(id+"F0.imprint","IMPRINT",EDGE,{"derivedFrom":subQ0}),-1.0]])]});}
            var Q1;
            Q1=makeQuery(id+"F0.imprint","IMPRINT",FACE,{"disambiguationData":[TD([[makeQuery(id+"F0.imprint","IMPRINT",EDGE,{"derivedFrom":sQuery(id+"F0.wireOp",EDGE,"E22.bottom")}),-1.0]])]});
            var Q2;
            {var subQ5=sQuery(id+"F0.wireOp",EDGE,"E20.top");Q2=makeQuery(id+"F0.imprint","IMPRINT",FACE,{"disambiguationData":[TD([[makeQuery(id+"F0.imprint","IMPRINT",EDGE,{"derivedFrom":subQ5}),1.0]])]});}
            var Q3;
            {var subQ3=sQuery(id+"F0.wireOp",EDGE,"E21.top");Q3=makeQuery(id+"F0.imprint","IMPRINT",FACE,{"disambiguationData":[TD([[makeQuery(id+"F0.imprint","IMPRINT",EDGE,{"derivedFrom":subQ3}),1.0]])]});}
            var Q4;
            {var subQ0=sQuery(id+"F0.wireOp",EDGE,"E22.top");Q4=makeQuery(id+"F0.imprint","IMPRINT",FACE,{"disambiguationData":[TD([[makeQuery(id+"F0.imprint","IMPRINT",EDGE,{"derivedFrom":subQ0}),-1.0]])]});}
            var Q5;
            {var subQ0=sQuery(id+"F0.wireOp",EDGE,"E20.left");var subQ1=sQuery(id+"F0.wireOp",EDGE,"a3aYjSOv-KGgK-Pzp2-STLL-ZoR566E2SG2L");var subQ2=makeQuery(id+"F0.imprint","INTERSECT",VERTEX,{"derivedFrom":[subQ1,subQ0]});Q5=makeQuery(id+"F0.imprint","IMPRINT",FACE,{"disambiguationData":[TD([[makeQuery(id+"F0.imprint","IMPRINT",EDGE,{"disambiguationData":[TD([[subQ2,-1.0]])],"derivedFrom":subQ1}),-1.0]])]});}
            var Q6;
            {var subQ0=sQuery(id+"F0.wireOp",EDGE,"E20.left");var subQ1=sQuery(id+"F0.wireOp",EDGE,"WXd5efYa-JbfL-IF1L-SslL-BDGKgb6K0dqY");var subQ2=makeQuery(id+"F0.imprint","INTERSECT",VERTEX,{"derivedFrom":[subQ1,subQ0]});Q6=makeQuery(id+"F0.imprint","IMPRINT",FACE,{"disambiguationData":[TD([[makeQuery(id+"F0.imprint","IMPRINT",EDGE,{"disambiguationData":[TD([[subQ2,-1.0]])],"derivedFrom":subQ1}),-1.0]])]});}
            var Q7;
            {var subQ0=sQuery(id+"F0.wireOp",EDGE,"E20.left");var subQ1=sQuery(id+"F0.wireOp",EDGE,"o5i0NS2g-xdNk-XHE3-dkdj-B6CzDAg9Y3Px");var subQ2=makeQuery(id+"F0.imprint","INTERSECT",VERTEX,{"derivedFrom":[subQ1,subQ0]});Q7=makeQuery(id+"F0.imprint","IMPRINT",FACE,{"disambiguationData":[TD([[makeQuery(id+"F0.imprint","IMPRINT",EDGE,{"disambiguationData":[TD([[subQ2,-1.0]])],"derivedFrom":subQ1}),-1.0]])]});}
            var Q8;
            {var subQ5=sQuery(id+"F0.wireOp",EDGE,"E20.bottom");Q8=makeQuery(id+"F0.imprint","IMPRINT",FACE,{"disambiguationData":[TD([[makeQuery(id+"F0.imprint","IMPRINT",EDGE,{"derivedFrom":subQ5}),-1.0]])]});}
            var Q9;
            Q9=makeQuery(id+"F0.imprint","IMPRINT",FACE,{"disambiguationData":[TD([[makeQuery(id+"F0.imprint","IMPRINT",EDGE,{"derivedFrom":sQuery(id+"F0.wireOp",EDGE,"E21.bottom")}),1.0]])]});
            var Q10;
            {var subQ0=sQuery(id+"F0.wireOp",EDGE,"E22.left");Q10=makeQuery(id+"F0.imprint","IMPRINT",FACE,{"disambiguationData":[TD([[makeQuery(id+"F0.imprint","IMPRINT",EDGE,{"derivedFrom":subQ0}),1.0]])]});}
            var Q11;
            {var subQ0=sQuery(id+"F0.wireOp",EDGE,"E21.left");Q11=makeQuery(id+"F0.imprint","IMPRINT",FACE,{"disambiguationData":[TD([[makeQuery(id+"F0.imprint","IMPRINT",EDGE,{"derivedFrom":subQ0}),-1.0]])]});}
            extrude(context, id + "F5", {"entities" : qUnion([Q0, Q1, Q2, Q3, Q4, Q5, Q6, Q7, Q8, Q9, Q10, Q11]), "operationType" : NewBodyOperationType.ADD, "depth" : 6 * mm, "offsetDistance" : 25 * mm});
        }
        {
            var Q0;
            Q0=makeQuery(id+"F0.imprint","IMPRINT",FACE,{"disambiguationData":[TD([[makeQuery(id+"F0.imprint","IMPRINT",EDGE,{"derivedFrom":sQuery(id+"F0.wireOp",EDGE,"E20.left")}),1.0]])]});
            extrude(context, id + "F6", {"entities" : qUnion([Q0]), "operationType" : NewBodyOperationType.ADD, "depth" : 4 * mm, "offsetDistance" : 25 * mm});
        }
        {
            var Q0;
            Q0=makeQuery(id+"F4.opExtrude","SWEPT_FACE",FACE,{"disambiguationData":[OSD([sQuery(id+"F0.wireOp",EDGE,"E13.bottom")])]});
            var sketch = newSketch(context, id + "F7", { "sketchPlane" : qUnion([Q0])});
            skCircle(sketch, "E35", {"center": v(1.5, -9) * mm, "radius": 1.25 * mm});
            skSolve(sketch);
        }
        {
            var Q0;
            Q0=makeQuery(id+"F4.opExtrude","SWEPT_FACE",FACE,{"disambiguationData":[OSD([sQuery(id+"F0.wireOp",EDGE,"E13.top")])]});
            var sketch = newSketch(context, id + "F8", { "sketchPlane" : qUnion([Q0])});
            skCircle(sketch, "E36.0", {"center": v(1.5, 9) * mm, "radius": 1.25 * mm});
            skSolve(sketch);
        }
        {
            var Q0;
            Q0=makeQuery(id+"F7.imprint","IMPRINT",FACE,{"disambiguationData":[TD([[makeQuery(id+"F7.imprint","IMPRINT",EDGE,{"derivedFrom":sQuery(id+"F7.wireOp",EDGE,"6C2Oj5xt-2Gh9-WaU8-TKf0-sr2JQ6RzCmAd")}),1.0]])]});
            var Q1;
            Q1=makeQuery(id+"F7.imprint","IMPRINT",FACE,{"disambiguationData":[TD([[makeQuery(id+"F7.imprint","IMPRINT",EDGE,{"derivedFrom":sQuery(id+"F7.wireOp",EDGE,"E35")}),1.0]])]});
            var Q2;
            Q2=makeQuery(id+"F4.opExtrude","SWEPT_FACE",FACE,{"disambiguationData":[OSD([sQuery(id+"F0.wireOp",EDGE,"E30.trimOffspring")])]});
            extrude(context, id + "F9", {"entities" : qUnion([Q0, Q1]), "operationType" : NewBodyOperationType.REMOVE, "endBound" : BoundingType.UP_TO_SURFACE, "oppositeDirection" : true, "depth" : 25 * mm, "endBoundEntityFace" : qUnion([Q2]), "offsetDistance" : 25 * mm});
        }
        {
            var Q0;
            Q0 = qSketchRegion(id + "F8", true);
            var Q1;
            Q1=makeQuery(id+"F4.opExtrude","SWEPT_FACE",FACE,{"disambiguationData":[OSD([sQuery(id+"F0.wireOp",EDGE,"E31.trimOffspring")])]});
            extrude(context, id + "F10", {"entities" : qUnion([Q0]), "operationType" : NewBodyOperationType.REMOVE, "endBound" : BoundingType.UP_TO_SURFACE, "oppositeDirection" : true, "depth" : 25 * mm, "endBoundEntityFace" : qUnion([Q1]), "offsetDistance" : 25 * mm});
        }
        {
            var Q0;
            Q0=makeQuery(id+"F1.opExtrude","CAP_EDGE",EDGE,{"disambiguationData":[OSD([sQuery(id+"F0.wireOp",EDGE,"E0.top")])],"isStart":true});
            var Q1;
            {var subQ0=sQuery(id+"F0.wireOp",EDGE,"E0.left");var subQ1=sQuery(id+"F0.wireOp",EDGE,"E0.bottom");Q1=makeQuery(id+"FY22JhLRbqmVvaR_1.boolean.opBoolean","SPLIT",EDGE,{"disambiguationData":[TD([makeQuery(id+"F1.opExtrude","SWEPT_FACE",FACE,{"disambiguationData":[OSD([subQ0])]})])],"derivedFrom":makeQuery(id+"F1.opExtrude","CAP_EDGE",EDGE,{"disambiguationData":[OSD([subQ1])],"isStart":true})});}
            var Q2;
            {var subQ0=sQuery(id+"F0.wireOp",EDGE,"E0.right");var subQ1=sQuery(id+"F0.wireOp",EDGE,"E0.bottom");Q2=makeQuery(id+"FY22JhLRbqmVvaR_1.boolean.opBoolean","SPLIT",EDGE,{"disambiguationData":[TD([makeQuery(id+"F1.opExtrude","SWEPT_FACE",FACE,{"disambiguationData":[OSD([subQ0])]})])],"derivedFrom":makeQuery(id+"F1.opExtrude","CAP_EDGE",EDGE,{"disambiguationData":[OSD([subQ1])],"isStart":true})});}
            var Q3;
            Q3=makeQuery(id+"FY22JhLRbqmVvaR_1.boolean.opBoolean","SPLIT",EDGE,{"derivedFrom":makeQuery(id+"F1.opExtrude","CAP_EDGE",EDGE,{"disambiguationData":[OSD([sQuery(id+"F0.wireOp",EDGE,"E0.left")])],"isStart":true})});
            var Q4;
            Q4=makeQuery(id+"FY22JhLRbqmVvaR_1.boolean.opBoolean","SPLIT",EDGE,{"derivedFrom":makeQuery(id+"F1.opExtrude","CAP_EDGE",EDGE,{"disambiguationData":[OSD([sQuery(id+"F0.wireOp",EDGE,"E0.right")])],"isStart":true})});
            chamfer(context, id + "F11", {"entities" : qUnion([Q0, Q1, Q2, Q3, Q4]), "width" : 2 * mm, "tangentPropagation" : true});
        }
        {
            var Q0;
            Q0=makeQuery(id+"F1.opExtrude","SWEPT_EDGE",EDGE,{"disambiguationData":[OSD([sQuery(id+"F0.wireOp",EDGE,"E0.bottom"),sQuery(id+"F0.wireOp",EDGE,"E0.right")])]});
            var Q1;
            Q1=makeQuery(id+"F1.opExtrude","SWEPT_EDGE",EDGE,{"disambiguationData":[OSD([sQuery(id+"F0.wireOp",EDGE,"E0.bottom"),sQuery(id+"F0.wireOp",EDGE,"E0.left")])]});
            var Q2;
            Q2=makeQuery(id+"F1.opExtrude","SWEPT_EDGE",EDGE,{"disambiguationData":[OSD([sQuery(id+"F0.wireOp",EDGE,"E0.top"),sQuery(id+"F0.wireOp",EDGE,"E0.right")])]});
            var Q3;
            Q3=makeQuery(id+"F1.opExtrude","SWEPT_EDGE",EDGE,{"disambiguationData":[OSD([sQuery(id+"F0.wireOp",EDGE,"E0.top"),sQuery(id+"F0.wireOp",EDGE,"E0.left")])]});
            var Q4;
            Q4=makeQuery(id+"F11.opChamfer","BLEND_EDGE",EDGE,{"blendedFrom":[makeQuery(id+"F1.opExtrude","CAP_EDGE",EDGE,{"disambiguationData":[OSD([sQuery(id+"F0.wireOp",EDGE,"E0.bottom")])],"isStart":true}),makeQuery(id+"F1.opExtrude","CAP_EDGE",EDGE,{"disambiguationData":[OSD([sQuery(id+"F0.wireOp",EDGE,"E0.left")])],"isStart":true})],"blendedInto":[]});
            var Q5;
            Q5=makeQuery(id+"F11.opChamfer","BLEND_EDGE",EDGE,{"blendedFrom":[makeQuery(id+"F1.opExtrude","CAP_EDGE",EDGE,{"disambiguationData":[OSD([sQuery(id+"F0.wireOp",EDGE,"E0.bottom")])],"isStart":true}),makeQuery(id+"F1.opExtrude","CAP_EDGE",EDGE,{"disambiguationData":[OSD([sQuery(id+"F0.wireOp",EDGE,"E0.right")])],"isStart":true})],"blendedInto":[]});
            var Q6;
            Q6=makeQuery(id+"F11.opChamfer","BLEND_EDGE",EDGE,{"blendedFrom":[makeQuery(id+"F1.opExtrude","CAP_EDGE",EDGE,{"disambiguationData":[OSD([sQuery(id+"F0.wireOp",EDGE,"E0.top")])],"isStart":true}),makeQuery(id+"F1.opExtrude","CAP_EDGE",EDGE,{"disambiguationData":[OSD([sQuery(id+"F0.wireOp",EDGE,"E0.right")])],"isStart":true})],"blendedInto":[]});
            var Q7;
            Q7=makeQuery(id+"F11.opChamfer","BLEND_EDGE",EDGE,{"blendedFrom":[makeQuery(id+"F1.opExtrude","CAP_EDGE",EDGE,{"disambiguationData":[OSD([sQuery(id+"F0.wireOp",EDGE,"E0.top")])],"isStart":true}),makeQuery(id+"F1.opExtrude","CAP_EDGE",EDGE,{"disambiguationData":[OSD([sQuery(id+"F0.wireOp",EDGE,"E0.left")])],"isStart":true})],"blendedInto":[]});
            fillet(context, id + "F12", {"entities" : qUnion([Q0, Q1, Q2, Q3, Q4, Q5, Q6, Q7]), "radius" : 5 * mm, "tangentPropagation" : true, "allowEdgeOverflow" : false});
        }
        {
            var Q0;
            Q0=makeQuery(id+"F3.opExtrude","CAP_FACE",FACE,{"disambiguationData":[OSD([sQuery(id+"F0.wireOp",EDGE,"E3"),sQuery(id+"F0.wireOp",EDGE,"E4")])],"isStart":false});
            var Q1;
            Q1=makeQuery(id+"F3.opExtrude","CAP_FACE",FACE,{"disambiguationData":[OSD([sQuery(id+"F0.wireOp",EDGE,"E5"),sQuery(id+"F0.wireOp",EDGE,"E6")])],"isStart":false});
            chamfer(context, id + "F13", {"entities" : qUnion([Q0, Q1]), "width" : 0.5 * mm, "tangentPropagation" : true});
        }
        {
            var Q0;
            Q0=makeQuery(id+"F4.opExtrude","SWEPT_EDGE",EDGE,{"disambiguationData":[OSD([sQuery(id+"F0.wireOp",EDGE,"E30.trimOffspring"),sQuery(id+"F0.wireOp",EDGE,"E32")])]});
            var Q1;
            Q1=makeQuery(id+"F4.opExtrude","SWEPT_EDGE",EDGE,{"disambiguationData":[OSD([sQuery(id+"F0.wireOp",EDGE,"E31.trimOffspring"),sQuery(id+"F0.wireOp",EDGE,"E34")])]});
            var Q2;
            Q2=makeQuery(id+"F4.opExtrude","SWEPT_EDGE",EDGE,{"disambiguationData":[OSD([sQuery(id+"F0.wireOp",EDGE,"E15"),sQuery(id+"F0.wireOp",EDGE,"E30.trimOffspring")])]});
            var Q3;
            Q3=makeQuery(id+"F4.opExtrude","SWEPT_EDGE",EDGE,{"disambiguationData":[OSD([sQuery(id+"F0.wireOp",EDGE,"E23.trimOffspring"),sQuery(id+"F0.wireOp",EDGE,"E31.trimOffspring")])]});
            var Q4;
            Q4=makeQuery(id+"F4.opExtrude","SWEPT_EDGE",EDGE,{"disambiguationData":[OSD([sQuery(id+"F0.wireOp",EDGE,"E21.right"),sQuery(id+"F0.wireOp",EDGE,"E25.trimOffspring")])]});
            var Q5;
            Q5=makeQuery(id+"F4.opExtrude","SWEPT_EDGE",EDGE,{"disambiguationData":[OSD([sQuery(id+"F0.wireOp",EDGE,"E22.right"),sQuery(id+"F0.wireOp",EDGE,"E26.trimOffspring")])]});
            var Q6;
            Q6=makeQuery(id+"F4.opExtrude","SWEPT_EDGE",EDGE,{"disambiguationData":[OSD([sQuery(id+"F0.wireOp",EDGE,"E14.right"),sQuery(id+"F0.wireOp",EDGE,"E25.trimOffspring")])]});
            var Q7;
            Q7=makeQuery(id+"F4.opExtrude","SWEPT_EDGE",EDGE,{"disambiguationData":[OSD([sQuery(id+"F0.wireOp",EDGE,"E14.right"),sQuery(id+"F0.wireOp",EDGE,"E26.trimOffspring")])]});
            fillet(context, id + "F14", {"entities" : qUnion([Q0, Q1, Q2, Q3, Q4, Q5, Q6, Q7]), "radius" : 2 * mm, "tangentPropagation" : true, "allowEdgeOverflow" : false});
        }
        {
            var Q0;
            {var subQ0=sQuery(id+"F0.wireOp",EDGE,"E24.trimOffspring");var subQ1=sQuery(id+"F0.wireOp",EDGE,"E28");Q0=makeQuery(id+"F12.opFillet","BLEND_EDGE",EDGE,{"blendedFrom":[makeQuery(id+"F11.opChamfer","BLEND_EDGE",EDGE,{"blendedFrom":[makeQuery(id+"F1.opExtrude","CAP_EDGE",EDGE,{"disambiguationData":[OSD([sQuery(id+"F0.wireOp",EDGE,"E0.bottom")])],"isStart":true}),makeQuery(id+"F1.opExtrude","CAP_EDGE",EDGE,{"disambiguationData":[OSD([sQuery(id+"F0.wireOp",EDGE,"E0.left")])],"isStart":true})],"blendedInto":[]}),makeQuery(id+"F5.boolean.opBoolean","MERGE",FACE,{"derivedFrom":[makeQuery(id+"F4.opExtrude","SWEPT_FACE",FACE,{"disambiguationData":[OSD([sQuery(id+"F0.wireOp",EDGE,"E13.bottom")])]}),makeQuery(id+"F4.opExtrude","SWEPT_FACE",FACE,{"disambiguationData":[OSD([subQ0]),TDD([makeQuery(id+"F0.imprint","IMPRINT",EDGE,{"disambiguationData":[TD([[makeQuery(id+"F0.imprint","INTERSECT",VERTEX,{"derivedFrom":[sQuery(id+"F0.wireOp",EDGE,"E21.right"),subQ0]}),1.0]])],"derivedFrom":subQ0})])]}),makeQuery(id+"F4.opExtrude","SWEPT_FACE",FACE,{"disambiguationData":[OSD([subQ0]),TDD([makeQuery(id+"F0.imprint","IMPRINT",EDGE,{"disambiguationData":[TD([[makeQuery(id+"F0.imprint","INTERSECT",VERTEX,{"derivedFrom":[sQuery(id+"F0.wireOp",EDGE,"E13.right"),subQ0]}),1.0]])],"derivedFrom":subQ0})])]}),makeQuery(id+"F4.opExtrude","SWEPT_FACE",FACE,{"disambiguationData":[OSD([sQuery(id+"F0.wireOp",EDGE,"E33")])]}),makeQuery(id+"F5.opExtrude","SWEPT_FACE",FACE,{"disambiguationData":[OSD([subQ0,subQ1])]}),makeQuery(id+"F5.opExtrude","SWEPT_FACE",FACE,{"disambiguationData":[OSD([subQ0])]})]})],"blendedInto":[makeQuery(id+"F5.boolean.opBoolean","MERGE",FACE,{"derivedFrom":[makeQuery(id+"F4.opExtrude","SWEPT_FACE",FACE,{"disambiguationData":[OSD([sQuery(id+"F0.wireOp",EDGE,"E13.bottom")])]}),makeQuery(id+"F4.opExtrude","SWEPT_FACE",FACE,{"disambiguationData":[OSD([subQ0]),TDD([makeQuery(id+"F0.imprint","IMPRINT",EDGE,{"disambiguationData":[TD([[makeQuery(id+"F0.imprint","INTERSECT",VERTEX,{"derivedFrom":[sQuery(id+"F0.wireOp",EDGE,"E21.right"),subQ0]}),1.0]])],"derivedFrom":subQ0})])]}),makeQuery(id+"F4.opExtrude","SWEPT_FACE",FACE,{"disambiguationData":[OSD([subQ0]),TDD([makeQuery(id+"F0.imprint","IMPRINT",EDGE,{"disambiguationData":[TD([[makeQuery(id+"F0.imprint","INTERSECT",VERTEX,{"derivedFrom":[sQuery(id+"F0.wireOp",EDGE,"E13.right"),subQ0]}),1.0]])],"derivedFrom":subQ0})])]}),makeQuery(id+"F4.opExtrude","SWEPT_FACE",FACE,{"disambiguationData":[OSD([sQuery(id+"F0.wireOp",EDGE,"E33")])]}),makeQuery(id+"F5.opExtrude","SWEPT_FACE",FACE,{"disambiguationData":[OSD([subQ0,subQ1])]}),makeQuery(id+"F5.opExtrude","SWEPT_FACE",FACE,{"disambiguationData":[OSD([subQ0])]})]})]});}
            var Q1;
            Q1=makeQuery(id+"F4.opExtrude","CAP_EDGE",EDGE,{"disambiguationData":[OSD([sQuery(id+"F0.wireOp",EDGE,"E13.left")])],"isStart":true});
            var Q2;
            Q2=makeQuery(id+"F4.opExtrude","CAP_EDGE",EDGE,{"disambiguationData":[OSD([sQuery(id+"F0.wireOp",EDGE,"E13.right")])],"isStart":true});
            var Q3;
            {var subQ0=sQuery(id+"F0.wireOp",EDGE,"E27.trimOffspring");var subQ1=sQuery(id+"F0.wireOp",EDGE,"E29");var subQ2=makeQuery(id+"F0.imprint","IMPRINT",VERTEX,{"derivedFrom":subQ0});Q3=makeQuery(id+"F5.boolean.opBoolean","MERGE",EDGE,{"derivedFrom":[makeQuery(id+"F4.opExtrude","CAP_EDGE",EDGE,{"disambiguationData":[OSD([sQuery(id+"F0.wireOp",EDGE,"E13.top")])],"isStart":true}),makeQuery(id+"F4.opExtrude","CAP_EDGE",EDGE,{"disambiguationData":[OSD([subQ0]),TDD([makeQuery(id+"F0.imprint","IMPRINT",EDGE,{"disambiguationData":[TD([[makeQuery(id+"F0.imprint","INTERSECT",VERTEX,{"derivedFrom":[sQuery(id+"F0.wireOp",EDGE,"E22.right"),subQ0]}),1.0]])],"derivedFrom":subQ0})])],"isStart":true}),makeQuery(id+"F4.opExtrude","CAP_EDGE",EDGE,{"disambiguationData":[OSD([subQ0]),TDD([makeQuery(id+"F0.imprint","IMPRINT",EDGE,{"disambiguationData":[TD([[subQ2,1.0]])],"derivedFrom":subQ0}),makeQuery(id+"F0.imprint","IMPRINT",EDGE,{"disambiguationData":[TD([[subQ2,-1.0]])],"derivedFrom":subQ0})])],"isStart":true}),makeQuery(id+"F4.opExtrude","CAP_EDGE",EDGE,{"disambiguationData":[OSD([subQ0]),TDD([makeQuery(id+"F0.imprint","IMPRINT",EDGE,{"disambiguationData":[TD([[makeQuery(id+"F0.imprint","INTERSECT",VERTEX,{"derivedFrom":[sQuery(id+"F0.wireOp",EDGE,"E13.right"),subQ0]}),1.0]])],"derivedFrom":subQ0})])],"isStart":true}),makeQuery(id+"F5.opExtrude","CAP_EDGE",EDGE,{"disambiguationData":[OSD([subQ0,subQ1])],"isStart":true}),makeQuery(id+"F5.opExtrude","CAP_EDGE",EDGE,{"disambiguationData":[OSD([subQ0])],"isStart":true})]});}
            fillet(context, id + "F15", {"entities" : qUnion([Q0, Q1, Q2, Q3]), "radius" : 2 * mm, "tangentPropagation" : true, "allowEdgeOverflow" : false});
        }
        {
            var Q0;
            Q0=makeQuery(id+"F4.opExtrude","CAP_FACE",FACE,{"disambiguationData":[OSD([sQuery(id+"F0.wireOp",EDGE,"E13.bottom"),sQuery(id+"F0.wireOp",EDGE,"E13.top"),sQuery(id+"F0.wireOp",EDGE,"E13.left"),sQuery(id+"F0.wireOp",EDGE,"E18"),sQuery(id+"F0.wireOp",EDGE,"E19"),sQuery(id+"F0.wireOp",EDGE,"E20.left")])],"isStart":false});
            var sketch = newSketch(context, id + "F16", { "sketchPlane" : qUnion([Q0])});
            skLineSegment(sketch, "E37.bottom", {"start": v(-15, 23) * mm, "end": v(15, 23) * mm});
            skLineSegment(sketch, "E37.top", {"start": v(-15, 6) * mm, "end": v(15, 6) * mm});
            skLineSegment(sketch, "E37.left", {"start": v(-15, 23) * mm, "end": v(-15, 6) * mm});
            skLineSegment(sketch, "E37.right", {"start": v(15, 23) * mm, "end": v(15, 6) * mm});
            skCircle(sketch, "E38.0", {"center": v(-11.5, 19) * mm, "radius": 1.25 * mm});
            skCircle(sketch, "E39.0", {"center": v(-11.5, 10) * mm, "radius": 1.25 * mm});
            skCircle(sketch, "E40.0", {"center": v(11.5, 10) * mm, "radius": 1.25 * mm});
            skCircle(sketch, "E41.0", {"center": v(11.5, 19) * mm, "radius": 1.25 * mm});
            skSolve(sketch);
        }
        {
            var Q0;
            Q0 = qSketchRegion(id + "F16", true);
            extrude(context, id + "F17", {"entities" : qUnion([Q0]), "depth" : 4 * mm, "offsetDistance" : 25 * mm});
        }
        {
            var Q0;
            Q0=makeQuery(id+"F17.opExtrude","SWEPT_FACE",FACE,{"disambiguationData":[OSD([sQuery(id+"F16.wireOp",EDGE,"E37.bottom")])]});
            var sketch = newSketch(context, id + "F18", { "sketchPlane" : qUnion([Q0])});
            skLineSegment(sketch, "E42.bottom", {"start": v(-8, -16) * mm, "end": v(8, -16) * mm});
            skLineSegment(sketch, "E42.top", {"start": v(-8, -28) * mm, "end": v(8, -28) * mm});
            skLineSegment(sketch, "E42.left", {"start": v(-8, -16) * mm, "end": v(-8, -28) * mm});
            skLineSegment(sketch, "E42.right", {"start": v(8, -16) * mm, "end": v(8, -28) * mm});
            skLineSegment(sketch, "E43.bottom", {"start": v(-4, -16) * mm, "end": v(4, -16) * mm});
            skLineSegment(sketch, "E43.top", {"start": v(-4, -24) * mm, "end": v(4, -24) * mm});
            skLineSegment(sketch, "E43.left", {"start": v(-4, -16) * mm, "end": v(-4, -24) * mm});
            skLineSegment(sketch, "E43.right", {"start": v(4, -16) * mm, "end": v(4, -24) * mm});
            skPoint(sketch, "E44", {"position": v(0, -16) * mm});
            skSolve(sketch);
        }
        {
            var Q0;
            Q0=makeQuery(id+"F18.imprint","IMPRINT",FACE,{"disambiguationData":[TD([[makeQuery(id+"F18.imprint","IMPRINT",EDGE,{"derivedFrom":sQuery(id+"F18.wireOp",EDGE,"E42.top")}),1.0]])]});
            extrude(context, id + "F19", {"entities" : qUnion([Q0]), "operationType" : NewBodyOperationType.ADD, "oppositeDirection" : true, "depth" : 8 * mm, "offsetDistance" : 25 * mm});
        }
        {
            var Q0;
            Q0=makeQuery(id+"F19.opExtrude","SWEPT_EDGE",EDGE,{"disambiguationData":[OSD([sQuery(id+"F18.wireOp",EDGE,"E42.top"),sQuery(id+"F18.wireOp",EDGE,"E42.left")])]});
            var Q1;
            Q1=makeQuery(id+"F19.opExtrude","SWEPT_EDGE",EDGE,{"disambiguationData":[OSD([sQuery(id+"F18.wireOp",EDGE,"E42.top"),sQuery(id+"F18.wireOp",EDGE,"E42.right")])]});
            var Q2;
            Q2=makeQuery(id+"F19.opExtrude","SWEPT_EDGE",EDGE,{"disambiguationData":[OSD([sQuery(id+"F18.wireOp",EDGE,"E43.top"),sQuery(id+"F18.wireOp",EDGE,"E43.right")])]});
            var Q3;
            Q3=makeQuery(id+"F19.opExtrude","SWEPT_EDGE",EDGE,{"disambiguationData":[OSD([sQuery(id+"F18.wireOp",EDGE,"E43.top"),sQuery(id+"F18.wireOp",EDGE,"E43.left")])]});
            fillet(context, id + "F20", {"entities" : qUnion([Q0, Q1, Q2, Q3]), "radius" : 2.5 * mm, "tangentPropagation" : true, "allowEdgeOverflow" : false});
        }
        {
            var Q0;
            {var subQ1=sQuery(id+"F16.wireOp",EDGE,"E37.left");var subQ2=sQuery(id+"F16.wireOp",EDGE,"E37.bottom");Q0=makeQuery(id+"F19.boolean.opBoolean","SPLIT",EDGE,{"disambiguationData":[TD([makeQuery(id+"F17.opExtrude","SWEPT_FACE",FACE,{"disambiguationData":[OSD([subQ1])]})])],"derivedFrom":makeQuery(id+"F17.opExtrude","CAP_EDGE",EDGE,{"disambiguationData":[OSD([subQ2])],"isStart":false})});}
            var Q1;
            Q1=makeQuery(id+"F17.opExtrude","CAP_EDGE",EDGE,{"disambiguationData":[OSD([sQuery(id+"F16.wireOp",EDGE,"E37.left")])],"isStart":false});
            var Q2;
            Q2=makeQuery(id+"F17.opExtrude","CAP_EDGE",EDGE,{"disambiguationData":[OSD([sQuery(id+"F16.wireOp",EDGE,"E37.right")])],"isStart":false});
            var Q3;
            {var subQ1=sQuery(id+"F16.wireOp",EDGE,"E37.right");var subQ2=sQuery(id+"F16.wireOp",EDGE,"E37.bottom");Q3=makeQuery(id+"F19.boolean.opBoolean","SPLIT",EDGE,{"disambiguationData":[TD([makeQuery(id+"F17.opExtrude","SWEPT_FACE",FACE,{"disambiguationData":[OSD([subQ1])]})])],"derivedFrom":makeQuery(id+"F17.opExtrude","CAP_EDGE",EDGE,{"disambiguationData":[OSD([subQ2])],"isStart":false})});}
            var Q4;
            Q4=makeQuery(id+"F17.opExtrude","CAP_EDGE",EDGE,{"disambiguationData":[OSD([sQuery(id+"F16.wireOp",EDGE,"E37.top")])],"isStart":false});
            var Q5;
            Q5=makeQuery(id+"F19.opExtrude","CAP_EDGE",EDGE,{"disambiguationData":[OSD([sQuery(id+"F18.wireOp",EDGE,"E42.left")])],"isStart":true});
            var Q6;
            Q6=makeQuery(id+"F19.opExtrude","CAP_EDGE",EDGE,{"disambiguationData":[OSD([sQuery(id+"F18.wireOp",EDGE,"E42.top")])],"isStart":false});
            var Q7;
            Q7=makeQuery(id+"F19.opExtrude","CAP_EDGE",EDGE,{"disambiguationData":[OSD([sQuery(id+"F18.wireOp",EDGE,"E43.right")])],"isStart":true});
            var Q8;
            {var subQ0=sQuery(id+"F18.wireOp",EDGE,"E43.left");var subQ1=sQuery(id+"F18.wireOp",EDGE,"E43.top");Q8=makeQuery(id+"F20.opFillet","BLEND_EDGE",EDGE,{"blendedFrom":[makeQuery(id+"F19.opExtrude","SWEPT_EDGE",EDGE,{"disambiguationData":[OSD([subQ1,subQ0])]}),makeQuery(id+"F19.opExtrude","CAP_FACE",FACE,{"disambiguationData":[OSD([sQuery(id+"F18.wireOp",EDGE,"E42.bottom"),sQuery(id+"F18.wireOp",EDGE,"E42.top"),sQuery(id+"F18.wireOp",EDGE,"E42.left"),sQuery(id+"F18.wireOp",EDGE,"E42.right"),subQ1,subQ0,sQuery(id+"F18.wireOp",EDGE,"E43.right")])],"isStart":false})],"blendedInto":[makeQuery(id+"F19.opExtrude","CAP_FACE",FACE,{"disambiguationData":[OSD([sQuery(id+"F18.wireOp",EDGE,"E42.bottom"),sQuery(id+"F18.wireOp",EDGE,"E42.top"),sQuery(id+"F18.wireOp",EDGE,"E42.left"),sQuery(id+"F18.wireOp",EDGE,"E42.right"),subQ1,subQ0,sQuery(id+"F18.wireOp",EDGE,"E43.right")])],"isStart":false})]});}
            chamfer(context, id + "F21", {"entities" : qUnion([Q0, Q1, Q2, Q3, Q4, Q5, Q6, Q7, Q8]), "width" : 1 * mm, "tangentPropagation" : true});
        }
    });
